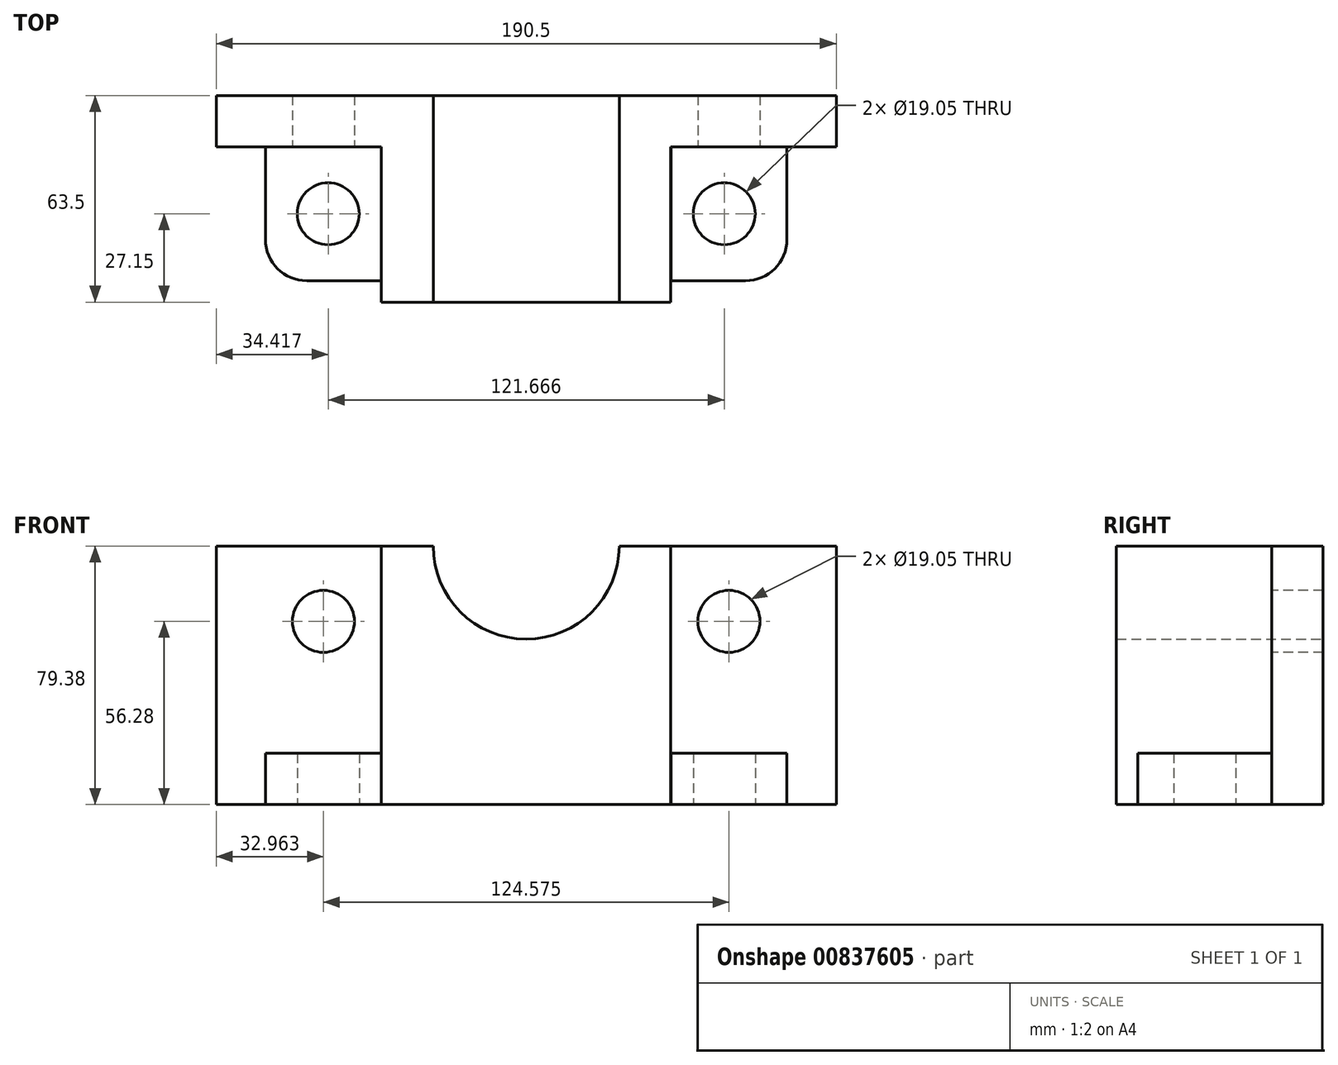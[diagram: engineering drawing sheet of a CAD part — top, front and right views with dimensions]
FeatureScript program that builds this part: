
annotation { "Feature Type Name" : "Feature", "Feature Type Description" : "" }
export const myFeature = defineFeature(function(context is Context, id is Id, definition is map)
    precondition{}
    {
        {
            var Q0;
            Q0=qCreatedBy(makeId("Front.planeOp"),FACE);
            var sketch = newSketch(context, id + "F0", { "sketchPlane" : qUnion([Q0])});
            skArc(sketch, "E0", {"start": v(-28.58, 0) * mm, "mid": v(0, -28.58) * mm, "end": v(28.58, 0) * mm});
            skLineSegment(sketch, "E1", {"start": v(-28.58, 0) * mm, "end": v(-95.25, 0) * mm});
            skLineSegment(sketch, "E2", {"start": v(-95.25, 0) * mm, "end": v(-95.25, -79.37) * mm});
            skLineSegment(sketch, "E3", {"start": v(-95.25, -79.37) * mm, "end": v(95.25, -79.37) * mm});
            skLineSegment(sketch, "E4", {"start": v(95.25, -79.37) * mm, "end": v(95.25, 0) * mm});
            skLineSegment(sketch, "E5", {"start": v(95.25, 0) * mm, "end": v(28.58, 0) * mm});
            skLineSegment(sketch, "E6", {"start": v(0, 0) * mm, "end": v(0, -60.72) * mm, "construction": true});
            skSolve(sketch);
        }
        {
            var Q0;
            Q0=makeQuery(id+"F0.imprint","IMPRINT",FACE,{"disambiguationData":[TD([[makeQuery(id+"F0.imprint","IMPRINT",EDGE,{"derivedFrom":sQuery(id+"F0.wireOp",EDGE,"E0")}),-1.0]])]});
            extrude(context, id + "F1", {"entities" : qUnion([Q0]), "depth" : 15.75 * mm, "offsetDistance" : 25.4 * mm});
        }
        {
            var Q0;
            Q0=makeQuery(id+"F1.opExtrude","CAP_FACE",FACE,{"disambiguationData":[OSD([sQuery(id+"F0.wireOp",EDGE,"E0"),sQuery(id+"F0.wireOp",EDGE,"E1"),sQuery(id+"F0.wireOp",EDGE,"E2"),sQuery(id+"F0.wireOp",EDGE,"E3"),sQuery(id+"F0.wireOp",EDGE,"E4"),sQuery(id+"F0.wireOp",EDGE,"E5")])],"isStart":false});
            var sketch = newSketch(context, id + "F2", { "sketchPlane" : qUnion([Q0])});
            skLineSegment(sketch, "E7", {"start": v(-44.47, 0) * mm, "end": v(-44.47, -79.37) * mm});
            skLineSegment(sketch, "E8", {"start": v(44.43, 0) * mm, "end": v(44.43, -79.37) * mm});
            skLineSegment(sketch, "E9", {"start": v(0, 0) * mm, "end": v(0, -79.37) * mm, "construction": true});
            skLineSegment(sketch, "E10", {"start": v(0, -79.37) * mm, "end": v(2.9, -79.37) * mm, "construction": true});
            skLineSegment(sketch, "E11.0", {"start": v(-28.58, 0) * mm, "end": v(-95.25, 0) * mm});
            skArc(sketch, "E11.2", {"start": v(-28.58, 0) * mm, "mid": v(0, -28.58) * mm, "end": v(28.58, 0) * mm});
            skLineSegment(sketch, "E11.3", {"start": v(95.25, 0) * mm, "end": v(28.58, 0) * mm});
            skLineSegment(sketch, "E11.5", {"start": v(-95.25, -79.37) * mm, "end": v(95.25, -79.37) * mm});
            skSolve(sketch);
        }
        {
            var Q0;
            {var subQ2=sQuery(id+"F2.wireOp",EDGE,"E7");Q0=makeQuery(id+"F2.imprint","IMPRINT",FACE,{"disambiguationData":[TD([[makeQuery(id+"F2.imprint","IMPRINT",EDGE,{"derivedFrom":subQ2}),1.0]])]});}
            var sketch = newSketch(context, id + "F3", { "sketchPlane" : qUnion([Q0])});
            skSolve(sketch);
        }
        {
            var Q0;
            Q0 = qSketchRegion(id + "F3", true);
            var Q1;
            {var subQ2=sQuery(id+"F2.wireOp",EDGE,"E7");Q1=makeQuery(id+"F2.imprint","IMPRINT",FACE,{"disambiguationData":[TD([[makeQuery(id+"F2.imprint","IMPRINT",EDGE,{"derivedFrom":subQ2}),1.0]])]});}
            extrude(context, id + "F4", {"entities" : qUnion([Q0, Q1]), "operationType" : NewBodyOperationType.ADD, "depth" : 47.75 * mm, "offsetDistance" : 25.4 * mm});
        }
        {
            var Q0;
            Q0=qCreatedBy(makeId("Top.planeOp"),FACE);
            cPlane(context, id + "F5", {"entities" : qUnion([Q0]), "cplaneType" : CPlaneType.OFFSET, "offset" : 79.38 * mm, "oppositeDirection" : true, "width" : 152.4 * mm, "height" : 152.4 * mm});
        }
        {
            var Q0;
            Q0=qCreatedBy(id+"F5.planeOp",FACE);
            var sketch = newSketch(context, id + "F6", { "sketchPlane" : qUnion([Q0])});
            skLineSegment(sketch, "E12.bottom", {"start": v(-80.1, -15.75) * mm, "end": v(-44.47, -15.75) * mm});
            skLineSegment(sketch, "E12.top", {"start": v(-67.4, -56.95) * mm, "end": v(-44.47, -56.95) * mm});
            skLineSegment(sketch, "E12.left", {"start": v(-80.1, -15.75) * mm, "end": v(-80.1, -44.25) * mm});
            skLineSegment(sketch, "E12.right", {"start": v(-44.47, -15.75) * mm, "end": v(-44.47, -56.95) * mm});
            skLineSegment(sketch, "E13", {"start": v(0, -71.7) * mm, "end": v(0, 17.7) * mm, "construction": true});
            skPoint(sketch, "E14.visualSharp", {"position": v(-80.1, -56.95) * mm});
            skArc(sketch, "E14.filletArc", {"start": v(-80.1, -44.25) * mm, "mid": v(-76.38, -53.23) * mm, "end": v(-67.4, -56.95) * mm});
            skCircle(sketch, "E15", {"center": v(-60.83, -36.35) * mm, "radius": 9.53 * mm});
            skPoint(sketch, "E15.centerSnap0", {"position": v(-44.47, -36.35) * mm});
            skPoint(sketch, "E16.MirrorP", {"position": v(44.47, -36.35) * mm});
            skCircle(sketch, "E17.MirrorC", {"center": v(60.83, -36.35) * mm, "radius": 9.53 * mm});
            skArc(sketch, "E18.MirrorCS", {"start": v(80.1, -44.25) * mm, "mid": v(76.38, -53.23) * mm, "end": v(67.4, -56.95) * mm});
            skLineSegment(sketch, "E19.MirrorCS", {"start": v(80.1, -15.75) * mm, "end": v(44.47, -15.75) * mm});
            skLineSegment(sketch, "E20.MirrorCS", {"start": v(44.47, -15.75) * mm, "end": v(44.47, -56.95) * mm});
            skLineSegment(sketch, "E21.MirrorCS", {"start": v(67.4, -56.95) * mm, "end": v(44.47, -56.95) * mm});
            skLineSegment(sketch, "E22.MirrorCS", {"start": v(80.1, -15.75) * mm, "end": v(80.1, -44.25) * mm});
            skPoint(sketch, "E23.MirrorP", {"position": v(80.1, -56.95) * mm});
            skSolve(sketch);
        }
        {
            var Q0;
            Q0 = qSketchRegion(id + "F6", true);
            extrude(context, id + "F7", {"entities" : qUnion([Q0]), "operationType" : NewBodyOperationType.ADD, "depth" : 15.75 * mm, "offsetDistance" : 25.4 * mm});
        }
        {
            var Q0;
            {var subQ0=sQuery(id+"F0.wireOp",EDGE,"E5");var subQ1=sQuery(id+"F0.wireOp",EDGE,"E4");var subQ2=sQuery(id+"F0.wireOp",EDGE,"E3");Q0=makeQuery(id+"F4.boolean.opBoolean","SPLIT",FACE,{"disambiguationData":[TD([makeQuery(id+"F1.opExtrude","SWEPT_FACE",FACE,{"disambiguationData":[OSD([subQ1])]})])],"derivedFrom":makeQuery(id+"F1.opExtrude","CAP_FACE",FACE,{"disambiguationData":[OSD([sQuery(id+"F0.wireOp",EDGE,"E0"),sQuery(id+"F0.wireOp",EDGE,"E1"),sQuery(id+"F0.wireOp",EDGE,"E2"),subQ2,subQ1,subQ0])],"isStart":false})});}
            var sketch = newSketch(context, id + "F8", { "sketchPlane" : qUnion([Q0])});
            skCircle(sketch, "E24", {"center": v(62.29, -23.1) * mm, "radius": 9.53 * mm});
            skPoint(sketch, "E24.centerSnap0", {"position": v(62.29, -63.63) * mm});
            skCircle(sketch, "E25.MirrorC", {"center": v(-62.29, -23.1) * mm, "radius": 9.53 * mm});
            skSolve(sketch);
        }
        {
            var Q0;
            Q0 = qSketchRegion(id + "F8", true);
            extrude(context, id + "F9", {"entities" : qUnion([Q0]), "operationType" : NewBodyOperationType.REMOVE, "oppositeDirection" : true, "depth" : 25.4 * mm, "offsetDistance" : 25.4 * mm});
        }
    });
